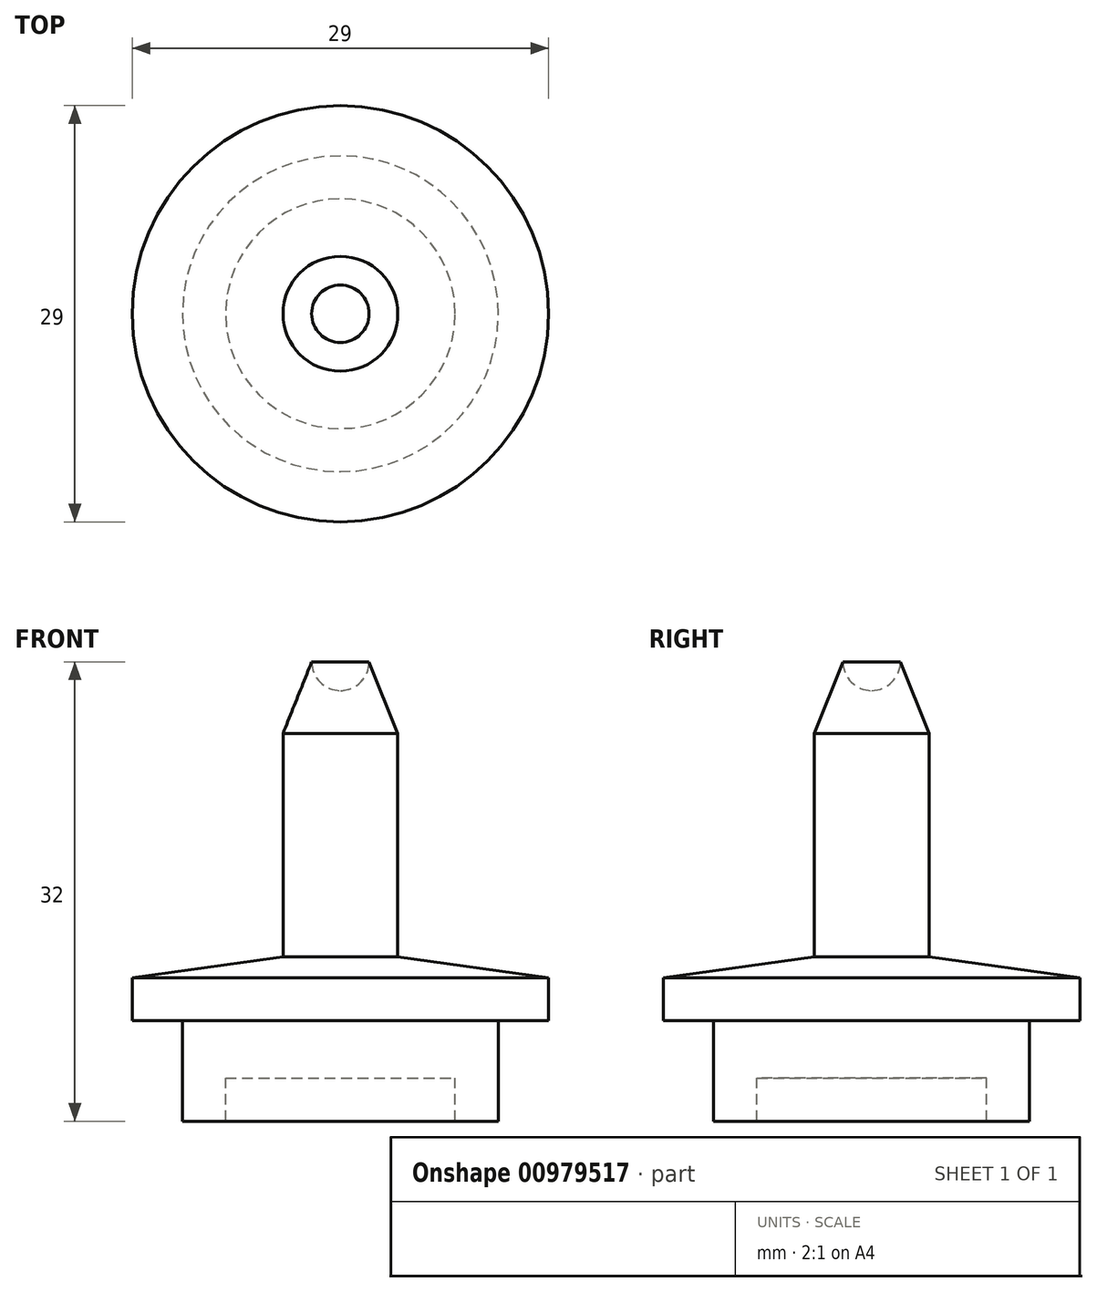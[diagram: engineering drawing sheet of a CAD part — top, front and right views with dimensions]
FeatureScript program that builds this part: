
annotation { "Feature Type Name" : "Feature", "Feature Type Description" : "" }
export const myFeature = defineFeature(function(context is Context, id is Id, definition is map)
    precondition{}
    {
        {
            var Q0;
            Q0=qCreatedBy(makeId("Front.planeOp"),FACE);
            var sketch = newSketch(context, id + "F0", { "sketchPlane" : qUnion([Q0])});
            skLineSegment(sketch, "E0", {"start": v(-11, 0) * mm, "end": v(-14.5, 0) * mm});
            skLineSegment(sketch, "E1", {"start": v(-14.5, 0) * mm, "end": v(-14.5, 3) * mm});
            skLineSegment(sketch, "E2", {"start": v(-11, 0) * mm, "end": v(-11, -7) * mm});
            skPoint(sketch, "E3.end.orphan", {"position": v(0, -2.83) * mm});
            skPoint(sketch, "E4.orphan", {"position": v(0, -2) * mm});
            skLineSegment(sketch, "E5", {"start": v(-14.5, 3) * mm, "end": v(-4, 4.45) * mm});
            skPoint(sketch, "E6.end.orphan", {"position": v(0, -3) * mm});
            skPoint(sketch, "E7.end.orphan", {"position": v(0, -4) * mm});
            skLineSegment(sketch, "E8", {"start": v(0, -4) * mm, "end": v(-8, -4) * mm});
            skLineSegment(sketch, "E9", {"start": v(-11, -7) * mm, "end": v(-8, -7) * mm});
            skLineSegment(sketch, "E10", {"start": v(-8, -4) * mm, "end": v(-8, -7) * mm});
            skLineSegment(sketch, "E11", {"start": v(-4, 4.45) * mm, "end": v(-4, 20) * mm});
            skArc(sketch, "E12", {"start": v(-2, 25) * mm, "mid": v(-1.41, 23.59) * mm, "end": v(0, 23) * mm});
            skLineSegment(sketch, "E13", {"start": v(-4, 20) * mm, "end": v(-2, 25) * mm});
            skLineSegment(sketch, "E14", {"start": v(0, 23) * mm, "end": v(0, -4) * mm});
            skSolve(sketch);
        }
        {
            var Q0;
            Q0=qCreatedBy(makeId("Top.planeOp"),FACE);
            var sketch = newSketch(context, id + "F1", { "sketchPlane" : qUnion([Q0])});
            skCircle(sketch, "E15", {"center": v(0, 0) * mm, "radius": 2.5 * mm});
            skSolve(sketch);
        }
        {
            var Q0;
            Q0=makeQuery(id+"F0.imprint","IMPRINT",FACE,{"disambiguationData":[TD([[makeQuery(id+"F0.imprint","IMPRINT",EDGE,{"derivedFrom":sQuery(id+"F0.wireOp",EDGE,"E0")}),-1.0]])]});
            var Q1;
            Q1 = qConstructionFilter(qBodyType(qCreatedBy(id + "F1" ,EDGE), BodyType.WIRE), ConstructionObject.NO);
            sweep(context, id + "F2", {"profiles" : qUnion([Q0]), "path" : qUnion([Q1])});
        }
    });
